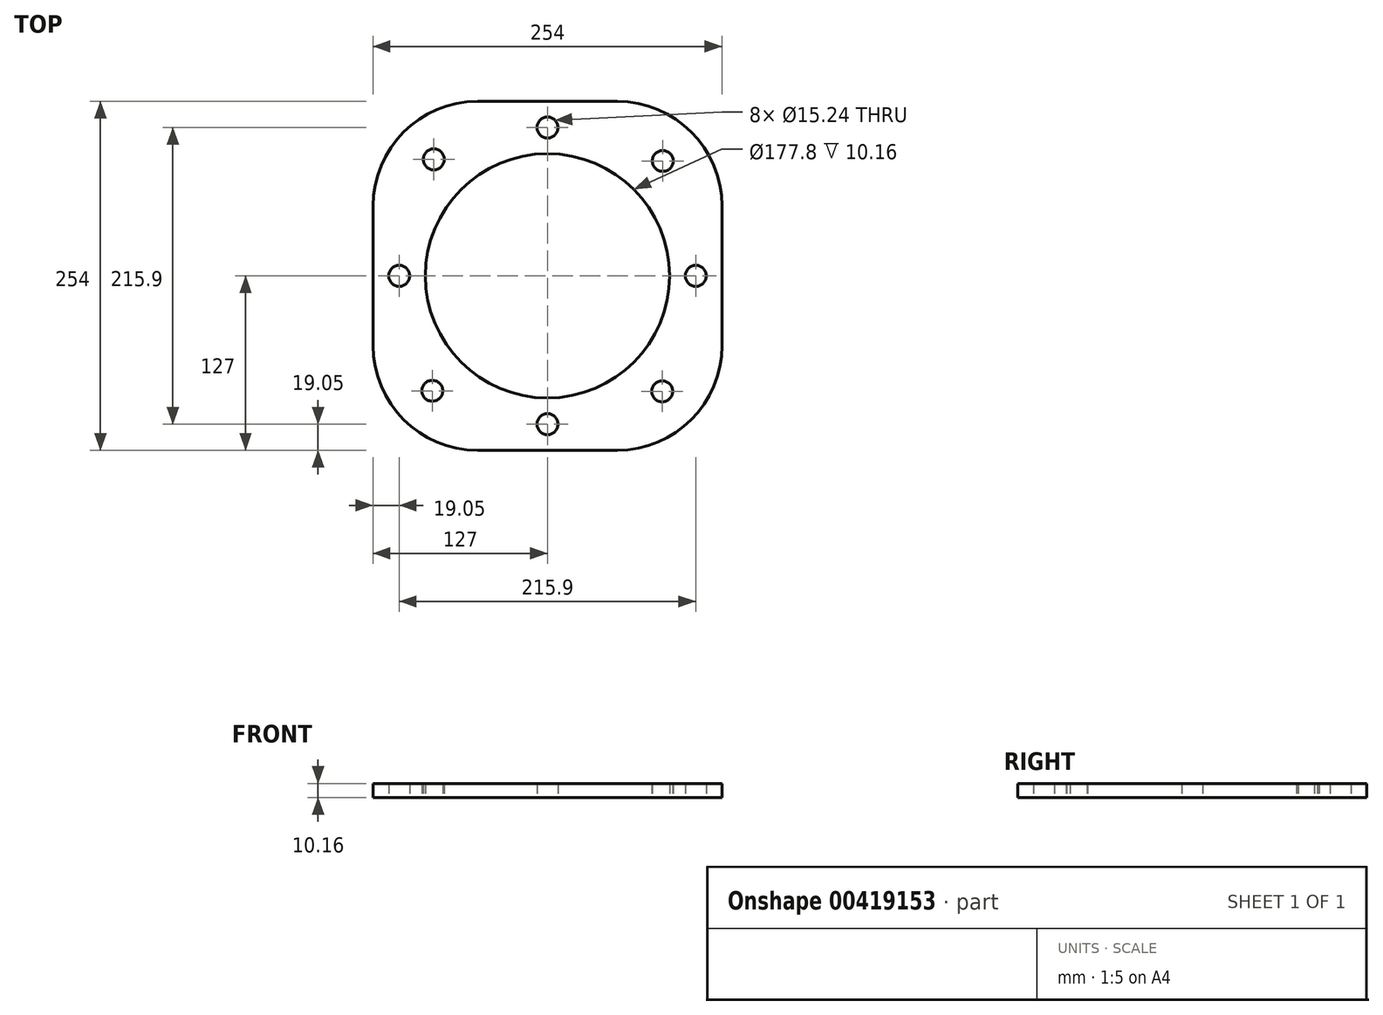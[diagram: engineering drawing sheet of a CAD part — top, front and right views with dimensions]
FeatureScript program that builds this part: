
annotation { "Feature Type Name" : "Feature", "Feature Type Description" : "" }
export const myFeature = defineFeature(function(context is Context, id is Id, definition is map)
    precondition{}
    {
        {
            var Q0;
            Q0=qCreatedBy(makeId("Top.planeOp"),FACE);
            var sketch = newSketch(context, id + "F0", { "sketchPlane" : qUnion([Q0])});
            skLineSegment(sketch, "E0.bottom", {"start": v(-50.8, -127) * mm, "end": v(50.8, -127) * mm});
            skLineSegment(sketch, "E0.top", {"start": v(-50.8, 127) * mm, "end": v(50.8, 127) * mm});
            skLineSegment(sketch, "E0.left", {"start": v(-127, -50.8) * mm, "end": v(-127, 50.8) * mm});
            skLineSegment(sketch, "E0.right", {"start": v(127, -50.8) * mm, "end": v(127, 50.8) * mm});
            skPoint(sketch, "E1.visualSharp", {"position": v(-127, 127) * mm});
            skArc(sketch, "E1.filletArc", {"start": v(-50.8, 127) * mm, "mid": v(-104.68, 104.68) * mm, "end": v(-127, 50.8) * mm});
            skPoint(sketch, "E2.visualSharp", {"position": v(127, 127) * mm});
            skArc(sketch, "E2.filletArc", {"start": v(127, 50.8) * mm, "mid": v(104.68, 104.68) * mm, "end": v(50.8, 127) * mm});
            skPoint(sketch, "E3.visualSharp", {"position": v(127, -127) * mm});
            skArc(sketch, "E3.filletArc", {"start": v(50.8, -127) * mm, "mid": v(104.68, -104.68) * mm, "end": v(127, -50.8) * mm});
            skPoint(sketch, "E4.visualSharp", {"position": v(-127, -127) * mm});
            skArc(sketch, "E4.filletArc", {"start": v(-127, -50.8) * mm, "mid": v(-104.68, -104.68) * mm, "end": v(-50.8, -127) * mm});
            skCircle(sketch, "E5", {"center": v(0, 0) * mm, "radius": 88.9 * mm});
            skLineSegment(sketch, "E6", {"start": v(0, 0) * mm, "end": v(-127, 0) * mm});
            skPoint(sketch, "E7", {"position": v(0, 88.9) * mm});
            skPoint(sketch, "E8", {"position": v(0, -88.9) * mm});
            skCircle(sketch, "E9", {"center": v(-83.86, -83.69) * mm, "radius": 7.62 * mm});
            skLineSegment(sketch, "E10", {"start": v(-63.03, -62.69) * mm, "end": v(-104.68, -104.68) * mm});
            skLineSegment(sketch, "E11", {"start": v(63.16, 62.56) * mm, "end": v(104.68, 104.68) * mm});
            skLineSegment(sketch, "E12", {"start": v(-60.8, 64.86) * mm, "end": v(-104.68, 104.68) * mm});
            skLineSegment(sketch, "E13", {"start": v(62.32, -63.4) * mm, "end": v(104.68, -104.68) * mm});
            skLineSegment(sketch, "E14", {"start": v(88.9, 0) * mm, "end": v(127, 0) * mm});
            skLineSegment(sketch, "E15", {"start": v(-88.9, 0) * mm, "end": v(-127, 0) * mm});
            skCircle(sketch, "E16", {"center": v(83.5, -84.04) * mm, "radius": 7.62 * mm});
            skCircle(sketch, "E17", {"center": v(83.92, 83.62) * mm, "radius": 7.62 * mm});
            skCircle(sketch, "E18", {"center": v(-82.74, 84.77) * mm, "radius": 7.62 * mm});
            skCircle(sketch, "E19", {"center": v(-107.95, 0) * mm, "radius": 7.62 * mm});
            skCircle(sketch, "E20", {"center": v(107.95, 0) * mm, "radius": 7.62 * mm});
            skCircle(sketch, "E21", {"center": v(0, 107.95) * mm, "radius": 7.62 * mm});
            skCircle(sketch, "E22", {"center": v(0, -107.95) * mm, "radius": 7.62 * mm});
            skPoint(sketch, "E23", {"position": v(0, 127) * mm});
            skPoint(sketch, "E24", {"position": v(0, -127) * mm});
            skLineSegment(sketch, "E25", {"start": v(0, 88.9) * mm, "end": v(0, 127) * mm});
            skLineSegment(sketch, "E26", {"start": v(0, -88.9) * mm, "end": v(0, -127) * mm});
            skSolve(sketch);
        }
        {
            var Q0;
            {var subQ6=sQuery(id+"F0.wireOp",EDGE,"E0.left");var subQ12=sQuery(id+"F0.wireOp",EDGE,"E1.filletArc");var subQ13=makeQuery(id+"F0.imprint","INTERSECT",VERTEX,{"derivedFrom":[subQ6,subQ12]});Q0=makeQuery(id+"F0.imprint","IMPRINT",FACE,{"disambiguationData":[TD([[makeQuery(id+"F0.imprint","IMPRINT",EDGE,{"disambiguationData":[TD([[subQ13,1.0]])],"derivedFrom":subQ6}),-1.0]])]});}
            var Q1;
            {var subQ5=sQuery(id+"F0.wireOp",EDGE,"E1.filletArc");var subQ6=sQuery(id+"F0.wireOp",EDGE,"E0.top");var subQ7=makeQuery(id+"F0.imprint","INTERSECT",VERTEX,{"derivedFrom":[subQ6,subQ5]});Q1=makeQuery(id+"F0.imprint","IMPRINT",FACE,{"disambiguationData":[TD([[makeQuery(id+"F0.imprint","IMPRINT",EDGE,{"disambiguationData":[TD([[subQ7,-1.0]])],"derivedFrom":subQ6}),-1.0]])]});}
            var Q2;
            {var subQ7=sQuery(id+"F0.wireOp",EDGE,"E2.filletArc");var subQ8=sQuery(id+"F0.wireOp",EDGE,"E0.top");var subQ9=makeQuery(id+"F0.imprint","INTERSECT",VERTEX,{"derivedFrom":[subQ8,subQ7]});Q2=makeQuery(id+"F0.imprint","IMPRINT",FACE,{"disambiguationData":[TD([[makeQuery(id+"F0.imprint","IMPRINT",EDGE,{"disambiguationData":[TD([[subQ9,1.0]])],"derivedFrom":subQ8}),-1.0]])]});}
            var Q3;
            {var subQ5=sQuery(id+"F0.wireOp",EDGE,"E2.filletArc");var subQ6=sQuery(id+"F0.wireOp",EDGE,"E0.right");var subQ7=makeQuery(id+"F0.imprint","INTERSECT",VERTEX,{"derivedFrom":[subQ6,subQ5]});Q3=makeQuery(id+"F0.imprint","IMPRINT",FACE,{"disambiguationData":[TD([[makeQuery(id+"F0.imprint","IMPRINT",EDGE,{"disambiguationData":[TD([[subQ7,1.0]])],"derivedFrom":subQ6}),1.0]])]});}
            var Q4;
            {var subQ5=sQuery(id+"F0.wireOp",EDGE,"E3.filletArc");var subQ6=sQuery(id+"F0.wireOp",EDGE,"E0.right");var subQ7=makeQuery(id+"F0.imprint","INTERSECT",VERTEX,{"derivedFrom":[subQ6,subQ5]});Q4=makeQuery(id+"F0.imprint","IMPRINT",FACE,{"disambiguationData":[TD([[makeQuery(id+"F0.imprint","IMPRINT",EDGE,{"disambiguationData":[TD([[subQ7,-1.0]])],"derivedFrom":subQ6}),1.0]])]});}
            var Q5;
            {var subQ11=sQuery(id+"F0.wireOp",EDGE,"E3.filletArc");var subQ12=sQuery(id+"F0.wireOp",EDGE,"E0.bottom");var subQ13=makeQuery(id+"F0.imprint","INTERSECT",VERTEX,{"derivedFrom":[subQ12,subQ11]});Q5=makeQuery(id+"F0.imprint","IMPRINT",FACE,{"disambiguationData":[TD([[makeQuery(id+"F0.imprint","IMPRINT",EDGE,{"disambiguationData":[TD([[subQ13,1.0]])],"derivedFrom":subQ12}),1.0]])]});}
            var Q6;
            {var subQ8=sQuery(id+"F0.wireOp",EDGE,"E4.filletArc");var subQ9=sQuery(id+"F0.wireOp",EDGE,"E0.bottom");var subQ10=makeQuery(id+"F0.imprint","INTERSECT",VERTEX,{"derivedFrom":[subQ9,subQ8]});Q6=makeQuery(id+"F0.imprint","IMPRINT",FACE,{"disambiguationData":[TD([[makeQuery(id+"F0.imprint","IMPRINT",EDGE,{"disambiguationData":[TD([[subQ10,-1.0]])],"derivedFrom":subQ9}),1.0]])]});}
            var Q7;
            {var subQ8=sQuery(id+"F0.wireOp",EDGE,"E4.filletArc");var subQ9=sQuery(id+"F0.wireOp",EDGE,"E0.left");var subQ10=makeQuery(id+"F0.imprint","INTERSECT",VERTEX,{"derivedFrom":[subQ9,subQ8]});Q7=makeQuery(id+"F0.imprint","IMPRINT",FACE,{"disambiguationData":[TD([[makeQuery(id+"F0.imprint","IMPRINT",EDGE,{"disambiguationData":[TD([[subQ10,-1.0]])],"derivedFrom":subQ9}),-1.0]])]});}
            extrude(context, id + "F1", {"entities" : qUnion([Q0, Q1, Q2, Q3, Q4, Q5, Q6, Q7]), "depth" : 10.16 * mm});
        }
    });
